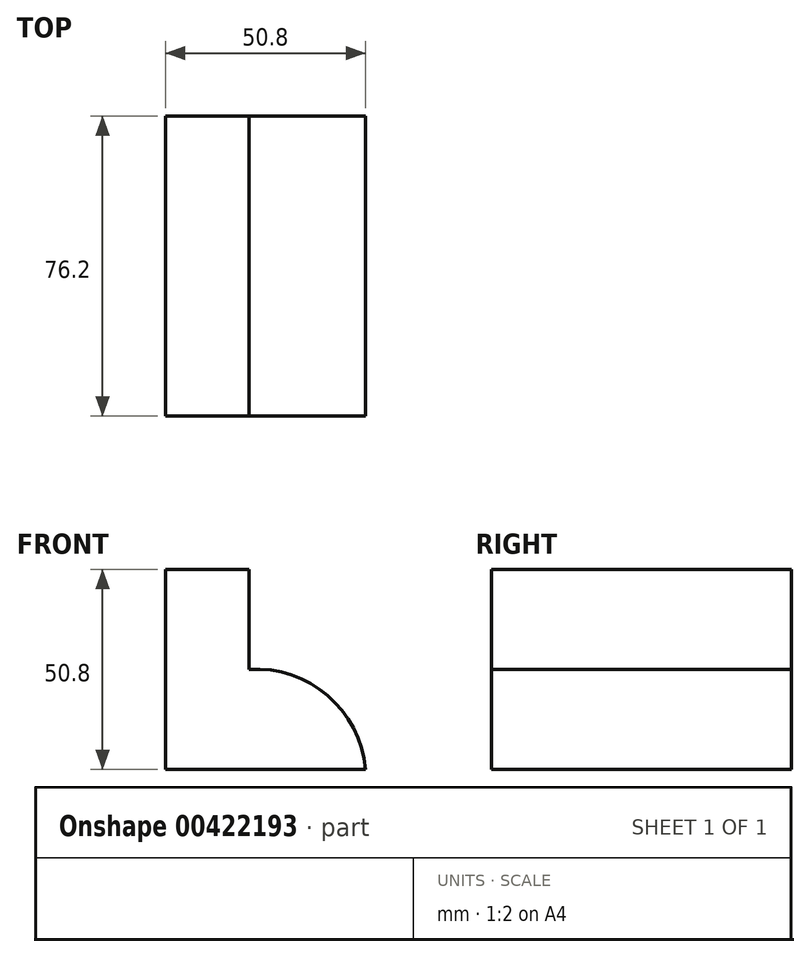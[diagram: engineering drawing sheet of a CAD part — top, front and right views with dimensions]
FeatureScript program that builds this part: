
annotation { "Feature Type Name" : "Feature", "Feature Type Description" : "" }
export const myFeature = defineFeature(function(context is Context, id is Id, definition is map)
    precondition{}
    {
        {
            var Q0;
            Q0=qCreatedBy(makeId("Front.planeOp"),FACE);
            var sketch = newSketch(context, id + "F0", { "sketchPlane" : qUnion([Q0])});
            skLineSegment(sketch, "E0", {"start": v(0, 0) * mm, "end": v(-50.8, 0) * mm});
            skLineSegment(sketch, "E1", {"start": v(-50.8, 0) * mm, "end": v(-50.8, 50.8) * mm});
            skLineSegment(sketch, "E2", {"start": v(-50.8, 50.8) * mm, "end": v(-29.61, 50.8) * mm});
            skLineSegment(sketch, "E3", {"start": v(-29.61, 25.4) * mm, "end": v(-29.61, 50.8) * mm});
            skArc(sketch, "E4", {"start": v(0, 0) * mm, "mid": v(-9.62, 18.75) * mm, "end": v(-29.61, 25.4) * mm});
            skSolve(sketch);
        }
        {
            var Q0;
            Q0 = qSketchRegion(id + "F0", true);
            extrude(context, id + "F1", {"entities" : qUnion([Q0]), "depth" : 76.2 * mm});
        }
    });
